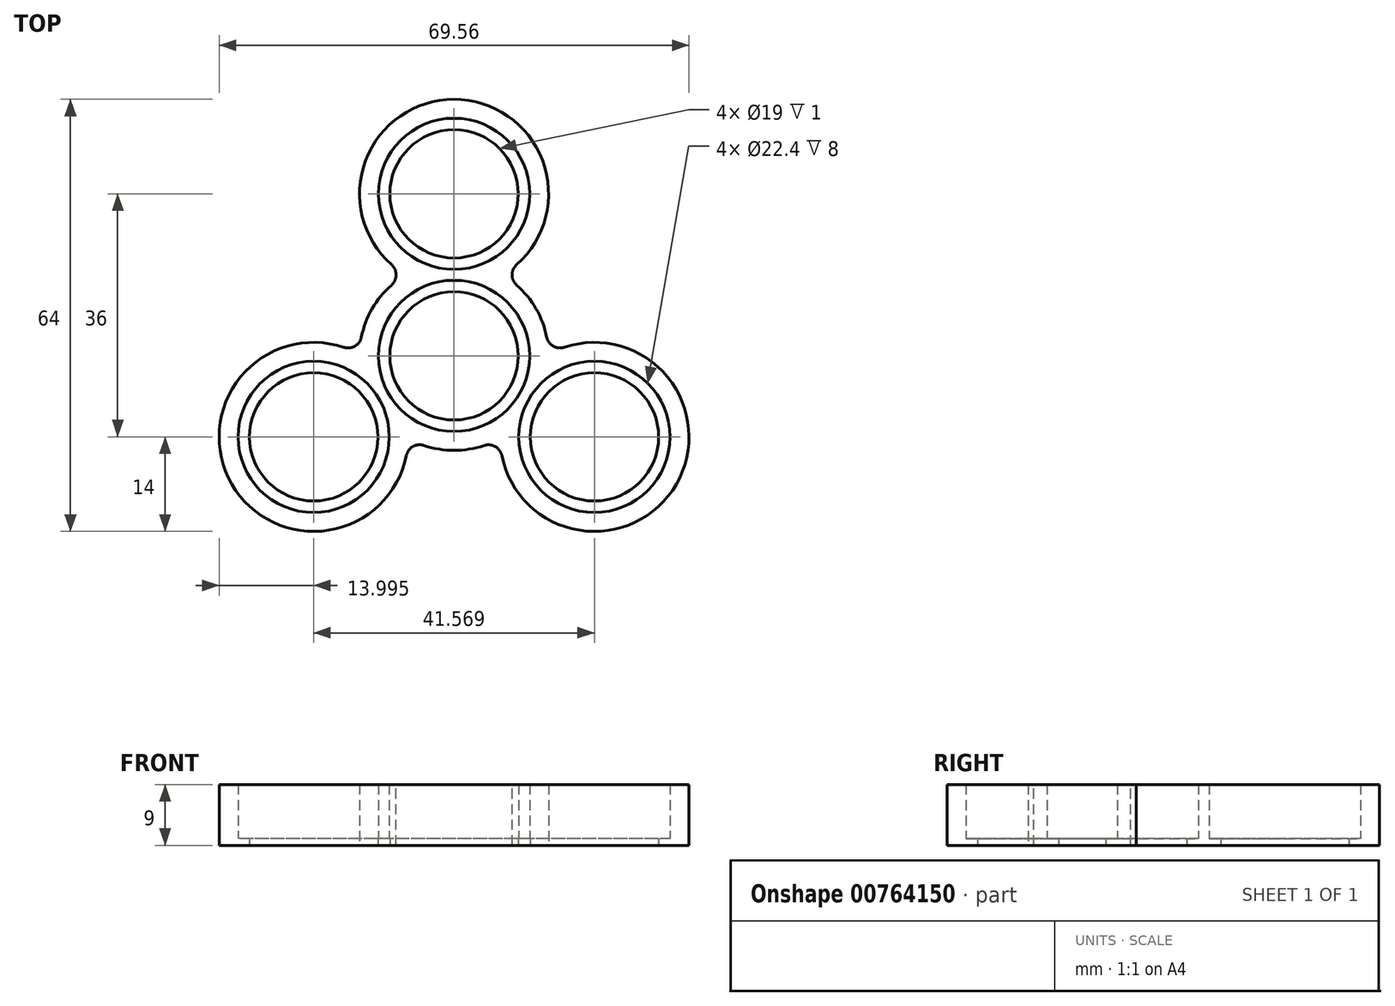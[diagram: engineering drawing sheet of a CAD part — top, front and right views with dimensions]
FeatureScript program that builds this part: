
annotation { "Feature Type Name" : "Feature", "Feature Type Description" : "" }
export const myFeature = defineFeature(function(context is Context, id is Id, definition is map)
    precondition{}
    {
        {
            var Q0;
            Q0=qCreatedBy(makeId("Top.planeOp"),FACE);
            var sketch = newSketch(context, id + "F0", { "sketchPlane" : qUnion([Q0])});
            skCircle(sketch, "E0", {"center": v(0, 0) * mm, "radius": 11.2 * mm});
            skCircle(sketch, "E1", {"center": v(0, 0) * mm, "radius": 14 * mm});
            skCircle(sketch, "E2", {"center": v(0, 24) * mm, "radius": 11.2 * mm});
            skCircle(sketch, "E3", {"center": v(0, 24) * mm, "radius": 14 * mm});
            skLineSegment(sketch, "E4", {"start": v(0, 24) * mm, "end": v(0, 0) * mm, "construction": true});
            skLineSegment(sketch, "E5", {"start": v(0, 0) * mm, "end": v(20.78, -12) * mm, "construction": true});
            skCircle(sketch, "E6", {"center": v(20.78, -12) * mm, "radius": 11.2 * mm});
            skCircle(sketch, "E7", {"center": v(20.78, -12) * mm, "radius": 14 * mm});
            skLineSegment(sketch, "E8", {"start": v(0, 0) * mm, "end": v(-20.78, -12) * mm, "construction": true});
            skCircle(sketch, "E9", {"center": v(-20.78, -12) * mm, "radius": 11.2 * mm});
            skCircle(sketch, "E10", {"center": v(-20.78, -12) * mm, "radius": 14 * mm});
            skCircle(sketch, "E11", {"center": v(0, 24) * mm, "radius": 9.5 * mm});
            skCircle(sketch, "E12", {"center": v(-20.78, -12) * mm, "radius": 9.5 * mm});
            skCircle(sketch, "E13", {"center": v(20.78, -12) * mm, "radius": 9.5 * mm});
            skCircle(sketch, "E14", {"center": v(0, 0) * mm, "radius": 9.5 * mm});
            skSolve(sketch);
        }
        {
            var Q0;
            Q0 = qSketchRegion(id + "F0", true);
            var Q1;
            Q1=makeQuery(id+"F0.imprint","IMPRINT",FACE,{"disambiguationData":[TD([[makeQuery(id+"F0.imprint","IMPRINT",EDGE,{"derivedFrom":sQuery(id+"F0.wireOp",EDGE,"E0")}),1.0]])]});
            var Q2;
            {var subQ0=sQuery(id+"F0.wireOp",EDGE,"E2");var subQ1=sQuery(id+"F0.wireOp",EDGE,"E1");var subQ2=makeQuery(id+"F0.imprint","INTERSECT",VERTEX,{"disambiguationData":[OD(0.0)],"derivedFrom":[subQ1,subQ0]});Q2=makeQuery(id+"F0.imprint","IMPRINT",FACE,{"disambiguationData":[TD([[makeQuery(id+"F0.imprint","IMPRINT",EDGE,{"disambiguationData":[TD([[subQ2,-1.0]])],"derivedFrom":subQ1}),1.0]])]});}
            var Q3;
            {var subQ0=sQuery(id+"F0.wireOp",EDGE,"E2");var subQ1=sQuery(id+"F0.wireOp",EDGE,"E1");var subQ2=makeQuery(id+"F0.imprint","INTERSECT",VERTEX,{"disambiguationData":[OD(0.0)],"derivedFrom":[subQ1,subQ0]});Q3=makeQuery(id+"F0.imprint","IMPRINT",FACE,{"disambiguationData":[TD([[makeQuery(id+"F0.imprint","IMPRINT",EDGE,{"disambiguationData":[TD([[subQ2,-1.0]])],"derivedFrom":subQ1}),-1.0]])]});}
            var Q4;
            {var subQ0=sQuery(id+"F0.wireOp",EDGE,"E9");var subQ1=sQuery(id+"F0.wireOp",EDGE,"E1");var subQ2=makeQuery(id+"F0.imprint","INTERSECT",VERTEX,{"disambiguationData":[OD(0.0)],"derivedFrom":[subQ1,subQ0]});Q4=makeQuery(id+"F0.imprint","IMPRINT",FACE,{"disambiguationData":[TD([[makeQuery(id+"F0.imprint","IMPRINT",EDGE,{"disambiguationData":[TD([[subQ2,-1.0]])],"derivedFrom":subQ1}),1.0]])]});}
            var Q5;
            {var subQ0=sQuery(id+"F0.wireOp",EDGE,"E9");var subQ1=sQuery(id+"F0.wireOp",EDGE,"E1");var subQ2=makeQuery(id+"F0.imprint","INTERSECT",VERTEX,{"disambiguationData":[OD(0.0)],"derivedFrom":[subQ1,subQ0]});Q5=makeQuery(id+"F0.imprint","IMPRINT",FACE,{"disambiguationData":[TD([[makeQuery(id+"F0.imprint","IMPRINT",EDGE,{"disambiguationData":[TD([[subQ2,-1.0]])],"derivedFrom":subQ1}),-1.0]])]});}
            var Q6;
            {var subQ0=sQuery(id+"F0.wireOp",EDGE,"E6");var subQ1=sQuery(id+"F0.wireOp",EDGE,"E1");var subQ2=makeQuery(id+"F0.imprint","INTERSECT",VERTEX,{"disambiguationData":[OD(0.0)],"derivedFrom":[subQ1,subQ0]});Q6=makeQuery(id+"F0.imprint","IMPRINT",FACE,{"disambiguationData":[TD([[makeQuery(id+"F0.imprint","IMPRINT",EDGE,{"disambiguationData":[TD([[subQ2,-1.0]])],"derivedFrom":subQ1}),1.0]])]});}
            var Q7;
            {var subQ0=sQuery(id+"F0.wireOp",EDGE,"E6");var subQ1=sQuery(id+"F0.wireOp",EDGE,"E1");var subQ2=makeQuery(id+"F0.imprint","INTERSECT",VERTEX,{"disambiguationData":[OD(0.0)],"derivedFrom":[subQ1,subQ0]});Q7=makeQuery(id+"F0.imprint","IMPRINT",FACE,{"disambiguationData":[TD([[makeQuery(id+"F0.imprint","IMPRINT",EDGE,{"disambiguationData":[TD([[subQ2,-1.0]])],"derivedFrom":subQ1}),-1.0]])]});}
            var Q8;
            {var subQ0=sQuery(id+"F0.wireOp",EDGE,"E10");var subQ1=sQuery(id+"F0.wireOp",EDGE,"E0");var subQ2=makeQuery(id+"F0.imprint","INTERSECT",VERTEX,{"disambiguationData":[OD(0.0)],"derivedFrom":[subQ1,subQ0]});Q8=makeQuery(id+"F0.imprint","IMPRINT",FACE,{"disambiguationData":[TD([[makeQuery(id+"F0.imprint","IMPRINT",EDGE,{"disambiguationData":[TD([[subQ2,-1.0]])],"derivedFrom":subQ1}),1.0]])]});}
            var Q9;
            {var subQ0=sQuery(id+"F0.wireOp",EDGE,"E7");var subQ1=sQuery(id+"F0.wireOp",EDGE,"E0");var subQ2=makeQuery(id+"F0.imprint","INTERSECT",VERTEX,{"disambiguationData":[OD(0.0)],"derivedFrom":[subQ1,subQ0]});Q9=makeQuery(id+"F0.imprint","IMPRINT",FACE,{"disambiguationData":[TD([[makeQuery(id+"F0.imprint","IMPRINT",EDGE,{"disambiguationData":[TD([[subQ2,-1.0]])],"derivedFrom":subQ1}),1.0]])]});}
            var Q10;
            {var subQ0=sQuery(id+"F0.wireOp",EDGE,"E3");var subQ1=sQuery(id+"F0.wireOp",EDGE,"E0");var subQ2=makeQuery(id+"F0.imprint","INTERSECT",VERTEX,{"disambiguationData":[OD(0.0)],"derivedFrom":[subQ1,subQ0]});Q10=makeQuery(id+"F0.imprint","IMPRINT",FACE,{"disambiguationData":[TD([[makeQuery(id+"F0.imprint","IMPRINT",EDGE,{"disambiguationData":[TD([[subQ2,1.0]])],"derivedFrom":subQ1}),1.0]])]});}
            extrude(context, id + "F1", {"entities" : qUnion([Q0, Q1, Q2, Q3, Q4, Q5, Q6, Q7, Q8, Q9, Q10]), "depth" : 1 * mm, "offsetDistance" : 25 * mm});
        }
        {
            var Q0;
            Q0 = qSketchRegion(id + "F0", true);
            extrude(context, id + "F2", {"entities" : qUnion([Q0]), "operationType" : NewBodyOperationType.ADD, "depth" : 9 * mm, "offsetDistance" : 25 * mm});
        }
        {
            var Q0;
            {var subQ0=sQuery(id+"F0.wireOp",EDGE,"E3");var subQ1=sQuery(id+"F0.wireOp",EDGE,"E1");var subQ2=makeQuery(id+"F0.imprint","INTERSECT",VERTEX,{"disambiguationData":[OD(1.0)],"derivedFrom":[subQ1,subQ0]});Q0=makeQuery(id+"F2.boolean.opBoolean","MERGE",EDGE,{"derivedFrom":[makeQuery(id+"F1.opExtrude","SWEPT_EDGE",EDGE,{"disambiguationData":[OSD([subQ1,subQ0]),TDD([subQ2])]}),makeQuery(id+"F2.opExtrude","SWEPT_EDGE",EDGE,{"disambiguationData":[OSD([subQ1,subQ0]),TDD([subQ2])]})]});}
            var Q1;
            {var subQ0=sQuery(id+"F0.wireOp",EDGE,"E10");var subQ1=sQuery(id+"F0.wireOp",EDGE,"E1");var subQ2=makeQuery(id+"F0.imprint","INTERSECT",VERTEX,{"disambiguationData":[OD(0.0)],"derivedFrom":[subQ1,subQ0]});Q1=makeQuery(id+"F2.boolean.opBoolean","MERGE",EDGE,{"derivedFrom":[makeQuery(id+"F1.opExtrude","SWEPT_EDGE",EDGE,{"disambiguationData":[OSD([subQ1,subQ0]),TDD([subQ2])]}),makeQuery(id+"F2.opExtrude","SWEPT_EDGE",EDGE,{"disambiguationData":[OSD([subQ1,subQ0]),TDD([subQ2])]})]});}
            var Q2;
            {var subQ0=sQuery(id+"F0.wireOp",EDGE,"E10");var subQ1=sQuery(id+"F0.wireOp",EDGE,"E1");var subQ2=makeQuery(id+"F0.imprint","INTERSECT",VERTEX,{"disambiguationData":[OD(1.0)],"derivedFrom":[subQ1,subQ0]});Q2=makeQuery(id+"F2.boolean.opBoolean","MERGE",EDGE,{"derivedFrom":[makeQuery(id+"F1.opExtrude","SWEPT_EDGE",EDGE,{"disambiguationData":[OSD([subQ1,subQ0]),TDD([subQ2])]}),makeQuery(id+"F2.opExtrude","SWEPT_EDGE",EDGE,{"disambiguationData":[OSD([subQ1,subQ0]),TDD([subQ2])]})]});}
            var Q3;
            {var subQ0=sQuery(id+"F0.wireOp",EDGE,"E7");var subQ1=sQuery(id+"F0.wireOp",EDGE,"E1");var subQ2=makeQuery(id+"F0.imprint","INTERSECT",VERTEX,{"disambiguationData":[OD(1.0)],"derivedFrom":[subQ1,subQ0]});Q3=makeQuery(id+"F2.boolean.opBoolean","MERGE",EDGE,{"derivedFrom":[makeQuery(id+"F1.opExtrude","SWEPT_EDGE",EDGE,{"disambiguationData":[OSD([subQ1,subQ0]),TDD([subQ2])]}),makeQuery(id+"F2.opExtrude","SWEPT_EDGE",EDGE,{"disambiguationData":[OSD([subQ1,subQ0]),TDD([subQ2])]})]});}
            var Q4;
            {var subQ0=sQuery(id+"F0.wireOp",EDGE,"E7");var subQ1=sQuery(id+"F0.wireOp",EDGE,"E1");var subQ2=makeQuery(id+"F0.imprint","INTERSECT",VERTEX,{"disambiguationData":[OD(0.0)],"derivedFrom":[subQ1,subQ0]});Q4=makeQuery(id+"F2.boolean.opBoolean","MERGE",EDGE,{"derivedFrom":[makeQuery(id+"F1.opExtrude","SWEPT_EDGE",EDGE,{"disambiguationData":[OSD([subQ1,subQ0]),TDD([subQ2])]}),makeQuery(id+"F2.opExtrude","SWEPT_EDGE",EDGE,{"disambiguationData":[OSD([subQ1,subQ0]),TDD([subQ2])]})]});}
            var Q5;
            {var subQ0=sQuery(id+"F0.wireOp",EDGE,"E3");var subQ1=sQuery(id+"F0.wireOp",EDGE,"E1");var subQ2=makeQuery(id+"F0.imprint","INTERSECT",VERTEX,{"disambiguationData":[OD(0.0)],"derivedFrom":[subQ1,subQ0]});Q5=makeQuery(id+"F2.boolean.opBoolean","MERGE",EDGE,{"derivedFrom":[makeQuery(id+"F1.opExtrude","SWEPT_EDGE",EDGE,{"disambiguationData":[OSD([subQ1,subQ0]),TDD([subQ2])]}),makeQuery(id+"F2.opExtrude","SWEPT_EDGE",EDGE,{"disambiguationData":[OSD([subQ1,subQ0]),TDD([subQ2])]})]});}
            fillet(context, id + "F3", {"entities" : qUnion([Q0, Q1, Q2, Q3, Q4, Q5]), "radius" : 2 * mm, "tangentPropagation" : true, "allowEdgeOverflow" : false});
        }
    });
